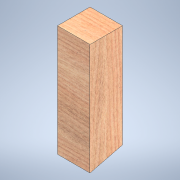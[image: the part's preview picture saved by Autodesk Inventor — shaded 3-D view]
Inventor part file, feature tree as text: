
AUTODESK INVENTOR PART (.ipt)
format: ipt  version: 2020.2 (Build 242310000, 310)  size: 119,296 bytes
history: native  units: in
note: dims shown in document units (in); Inventor stores cm internally (conversion verified against a paired STEP export)
features: extrude x1, sketch x1
ambient origin geometry x8: Origin, YZ Plane, XZ Plane, XY Plane, X Axis, Y Axis, Z Axis, Center Point
bodies: Solid1 (feature_tree)
feature tree (2):
  extrude  "Extrusion1"  TaperAngle=0.0deg  [1 undecoded]
  sketch  "Sketch1"  dims[d3=3.5in d4=0.0in]
note: 1 required parameter value undecoded (feature->parameter linkage not recoverable at this tier; creation-order binding heuristic only, values carry confidence <= 0.55)
